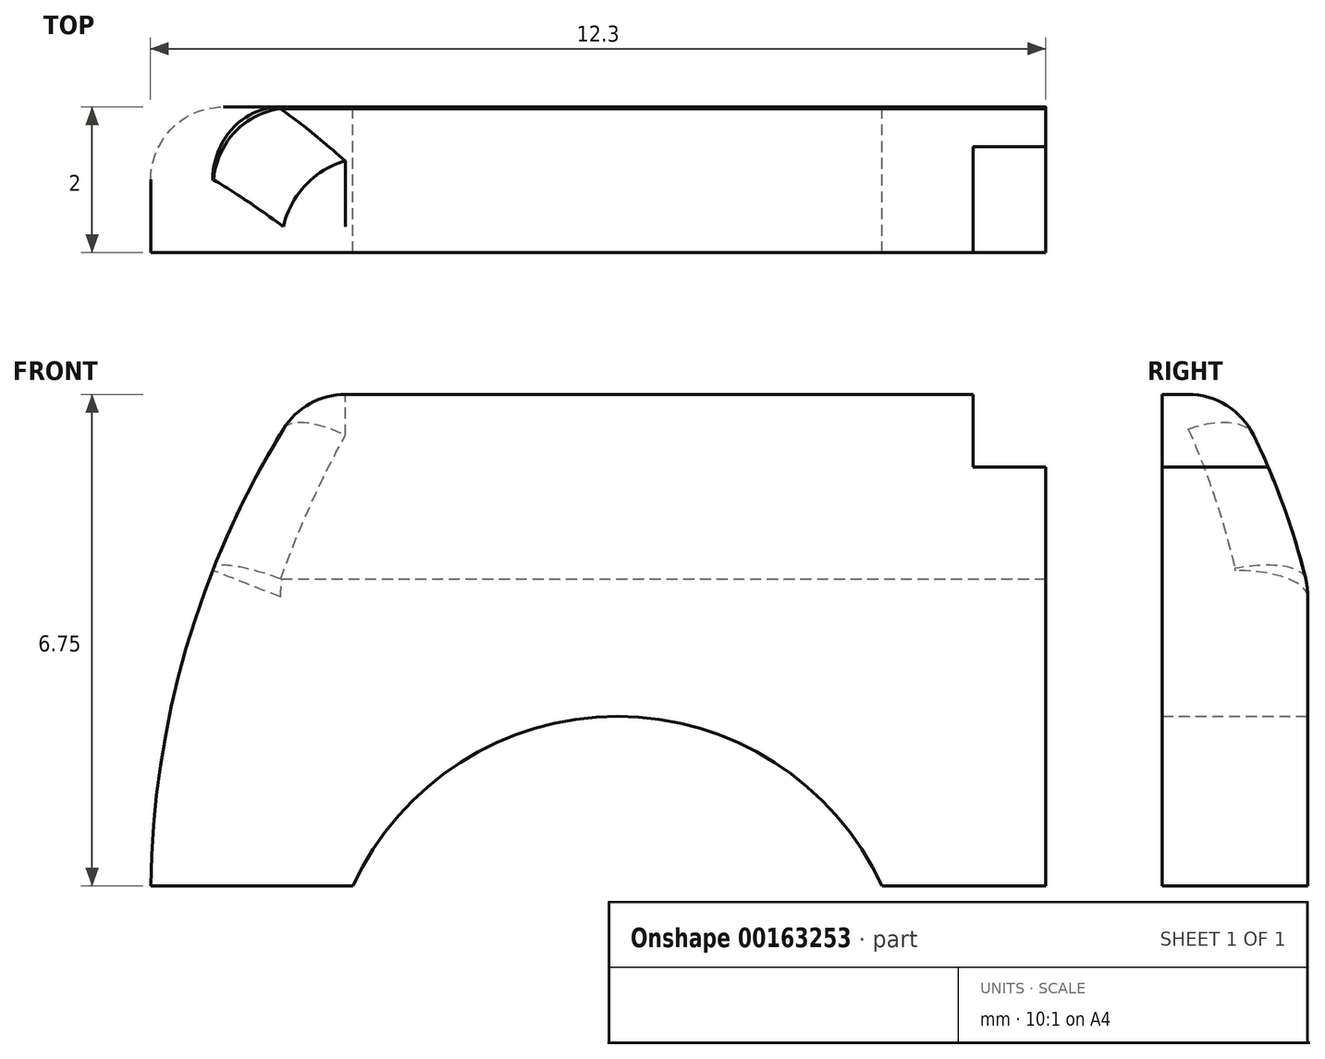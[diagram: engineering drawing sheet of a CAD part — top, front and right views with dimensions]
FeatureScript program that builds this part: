
annotation { "Feature Type Name" : "Feature", "Feature Type Description" : "" }
export const myFeature = defineFeature(function(context is Context, id is Id, definition is map)
    precondition{}
    {
        {
            var Q0;
            Q0=qCreatedBy(makeId("Front.planeOp"),FACE);
            var sketch = newSketch(context, id + "F0", { "sketchPlane" : qUnion([Q0])});
            skLineSegment(sketch, "E0", {"start": v(2.2, -0.4) * mm, "end": v(-0.58, -0.4) * mm});
            skArc(sketch, "E1", {"start": v(1.56, 6.34) * mm, "mid": v(0, 3.12) * mm, "end": v(-0.58, -0.4) * mm});
            skLineSegment(sketch, "E2", {"start": v(1.56, 6.34) * mm, "end": v(11.72, 6.34) * mm});
            skLineSegment(sketch, "E3", {"start": v(11.72, 6.34) * mm, "end": v(11.72, -0.4) * mm});
            skLineSegment(sketch, "E4", {"start": v(11.72, -0.4) * mm, "end": v(9.47, -0.4) * mm});
            skArc(sketch, "E5", {"start": v(9.47, -0.4) * mm, "mid": v(5.84, 1.92) * mm, "end": v(2.2, -0.4) * mm});
            skSolve(sketch);
        }
        {
            var Q0;
            Q0 = qSketchRegion(id + "F0", true);
            extrude(context, id + "F1", {"entities" : qUnion([Q0]), "depth" : 2 * mm});
        }
        {
            var Q0;
            Q0=makeQuery(id+"F1.opExtrude","SWEPT_FACE",FACE,{"disambiguationData":[OSD([sQuery(id+"F0.wireOp",EDGE,"E3")])]});
            var sketch = newSketch(context, id + "F2", { "sketchPlane" : qUnion([Q0])});
            skLineSegment(sketch, "E6.MirrorCS", {"start": v(15.38, 6.35) * mm, "end": v(15.38, 6.35) * mm});
            skArc(sketch, "E7.MirrorCS", {"start": v(-0.03, 3.8) * mm, "mid": v(0, 3.68) * mm, "end": v(0, 3.56) * mm});
            skArc(sketch, "E8.MirrorCS", {"start": v(-1.64, 7.27) * mm, "mid": v(-0.67, 5.62) * mm, "end": v(-0.03, 3.8) * mm});
            skPoint(sketch, "E9.MirrorP", {"position": v(-0.05, 3.55) * mm});
            skLineSegment(sketch, "E10.MirrorCS", {"start": v(1, 9.22) * mm, "end": v(-1.64, 7.27) * mm});
            skLineSegment(sketch, "E11.MirrorCS", {"start": v(2.2, 5.65) * mm, "end": v(1, 9.22) * mm});
            skLineSegment(sketch, "E12.MirrorCS", {"start": v(2.2, 5.65) * mm, "end": v(0, 3.56) * mm});
            skSolve(sketch);
        }
        {
            var Q0;
            Q0 = qSketchRegion(id + "F2", true);
            extrude(context, id + "F3", {"entities" : qUnion([Q0]), "operationType" : NewBodyOperationType.REMOVE, "endBound" : BoundingType.THROUGH_ALL, "oppositeDirection" : true, "depth" : 25 * mm});
        }
        {
            var Q0;
            Q0=makeQuery(id+"F3.boolean.opBoolean","INTERSECT",EDGE,{"derivedFrom":[makeQuery(id+"F1.opExtrude","SWEPT_FACE",FACE,{"disambiguationData":[OSD([sQuery(id+"F0.wireOp",EDGE,"E2")])]}),makeQuery(id+"F3.opExtrude","SWEPT_FACE",FACE,{"disambiguationData":[OSD([sQuery(id+"F2.wireOp",EDGE,"E8.MirrorCS")])]})]});
            fillet(context, id + "F4", {"entities" : qUnion([Q0]), "radius" : 1 * mm, "tangentPropagation" : true, "allowEdgeOverflow" : false});
        }
        {
            var Q0;
            Q0=makeQuery(id+"F1.opExtrude","SWEPT_EDGE",EDGE,{"disambiguationData":[OSD([sQuery(id+"F0.wireOp",EDGE,"E1"),sQuery(id+"F0.wireOp",EDGE,"E2")])]});
            var Q1;
            Q1=makeQuery(id+"F3.boolean.opBoolean","INTERSECT",EDGE,{"derivedFrom":[makeQuery(id+"F1.opExtrude","SWEPT_FACE",FACE,{"disambiguationData":[OSD([sQuery(id+"F0.wireOp",EDGE,"E1")])]}),makeQuery(id+"F3.opExtrude","SWEPT_FACE",FACE,{"disambiguationData":[OSD([sQuery(id+"F2.wireOp",EDGE,"E8.MirrorCS")])]})]});
            var Q2;
            Q2=makeQuery(id+"F1.opExtrude","CAP_EDGE",EDGE,{"disambiguationData":[OSD([sQuery(id+"F0.wireOp",EDGE,"E1")])],"isStart":true});
            fillet(context, id + "F5", {"entities" : qUnion([Q0, Q1, Q2]), "radius" : 1 * mm, "tangentPropagation" : true, "allowEdgeOverflow" : false});
        }
        {
            var Q0;
            Q0=makeQuery(id+"F1.opExtrude","SWEPT_FACE",FACE,{"disambiguationData":[OSD([sQuery(id+"F0.wireOp",EDGE,"E2")])]});
            var sketch = newSketch(context, id + "F6", { "sketchPlane" : qUnion([Q0])});
            skLineSegment(sketch, "E13.bottom", {"start": v(11.72, -2) * mm, "end": v(10.72, -2) * mm});
            skLineSegment(sketch, "E13.top", {"start": v(11.72, -0.03) * mm, "end": v(10.72, -0.03) * mm});
            skLineSegment(sketch, "E13.left", {"start": v(11.72, -2) * mm, "end": v(11.72, -0.03) * mm});
            skLineSegment(sketch, "E13.right", {"start": v(10.72, -2) * mm, "end": v(10.72, -0.03) * mm});
            skSolve(sketch);
        }
        {
            var Q0;
            Q0 = qSketchRegion(id + "F6", true);
            extrude(context, id + "F7", {"entities" : qUnion([Q0]), "operationType" : NewBodyOperationType.REMOVE, "oppositeDirection" : true, "depth" : 1 * mm});
        }
    });
